# Revit family: ASH_ArmitageShanks_WallHungHandRinseBasins_Contour21-S2154_500mm
name_source: partatom
category: Plumbing Fixtures
revit_build: Autodesk Revit MEP 2012 (Build: 20110309_2315(x64)
units: mm (PartAtom-declared; Revit-internal decimal feet)

## types (1)
- S215401 - Contour 21 back outlet washbasin, 50cm, no tapholes, no overflow, no chainstay hole
    Accessories = www.idealspec.co.uk
    AreaUnits = millimeters
    Assembly Code = C1030200
    AssetType = Fixed
    BIMObjectName = ASH_ArmitageShanks_WallHungHandRinseBasins_Contour21-S2154_500mm
    Brand = Armitage Shanks
    CWFU = 0
    CodePerformance = HTM64, Vitreous china to BS 3402
    Color = White
    ConnectionType = Plumbing
    Cost = 0 $
    Default Elevation = 800 mm  [stored 2.62467 ft]
    Description = Contour 21 back outlet washbasin, 50 cm, no tapholes, no overflow, no chainstay hole
    DrainSize = 32 mm  [stored 0.104987 ft]
    DurationUnit = year
    ECA = No
    ExpectedLife = 30
    Features = Back outlet washbasin, 50 cm, no tapholes, no overflow, no chainstay hole
    Finish = White
    HWFU = 0
    Help = www.idealspec.co.uk/contact-us.html
    IfcExportAs = IfcSanitaryType
    IfcExportType = WASHHANDBASIN
    InstallationInstructions = www.idealspec.co.uk/resources.html
    LinearUnits = millimeters
    ManufacturerURL = www.idealspec.co.uk
    Material = Vitreous china
    Model = S215401
    ModelNumber = S215401
    ModelReference = Contour 21 back outlet washbasin 50 cm
    NBSDescription = Wall hung hand rinse basins
    NBSReference = 45-35-70/368
    Name = WallHungHandRinseBasins_Contour21-S2154_50cm_ArmitageShanks
    NettWeight = 12.8 kg
    NominalDepth = 400 mm  [stored 1.31234 ft]
    NominalHeight = 187 mm
    NominalLength = 400 mm  [stored 1.31234 ft]
    NominalWidth = 506 mm
    ProductInformation = www.idealspec.co.uk/assets/datasheet/S215401
    Shape = Sculptured
    Size = 500 x 400 x 185 mm
    Space = Internal
    URL = www.idealspec.co.uk
    Uniclass2 = Pr_40_20_96_95
    Version = 1
    VolumeUnits = Litres
    WFU = 0
    WRAS = No
    WarrantyDescription = Manufacturers Warranty
    WarrantyDurationParts = 99
    WarrantyDurationUnit = year
    WashHandBasinMounting = Wall
    WashHandBasinType = Hand Rinse
    WaterEfficientProduct = No

note: [stored X ft] marks values corroborated as IEEE doubles in the binary element streams (Revit-internal decimal feet)

## geometry (parser evidence)
native form markers: Blend x10, Sweep x14
no freeform markers — native parametric forms only
